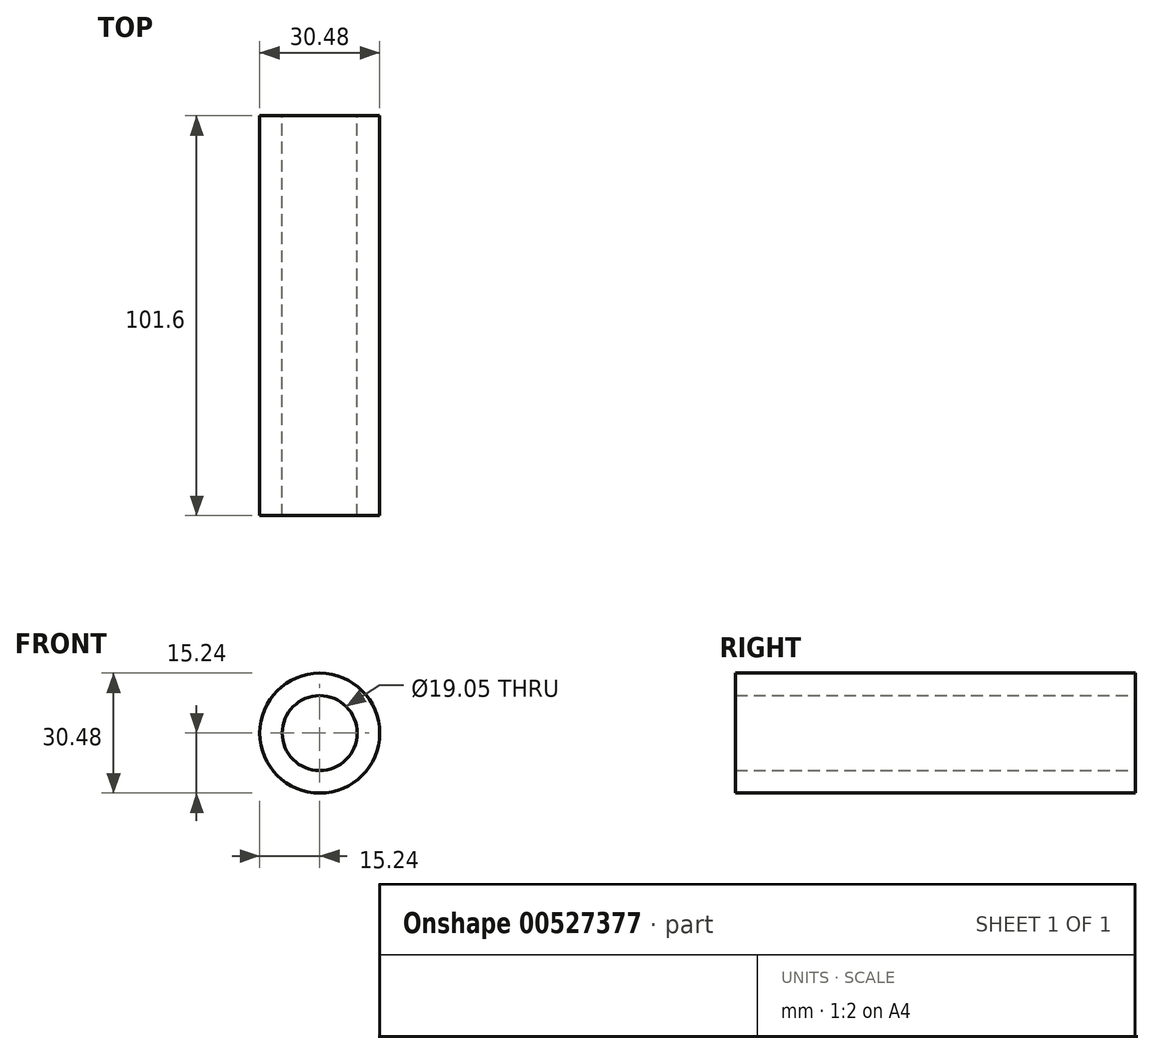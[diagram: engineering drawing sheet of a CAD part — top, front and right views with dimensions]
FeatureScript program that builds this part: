
annotation { "Feature Type Name" : "Feature", "Feature Type Description" : "" }
export const myFeature = defineFeature(function(context is Context, id is Id, definition is map)
    precondition{}
    {
        {
            var Q0;
            Q0=qCreatedBy(makeId("Front.planeOp"),FACE);
            var sketch = newSketch(context, id + "F0", { "sketchPlane" : qUnion([Q0])});
            skCircle(sketch, "E0", {"center": v(0, 0) * mm, "radius": 15.24 * mm});
            skCircle(sketch, "E1", {"center": v(0, 0) * mm, "radius": 9.53 * mm});
            skSolve(sketch);
        }
        {
            var Q0;
            Q0 = qSketchRegion(id + "F0", true);
            extrude(context, id + "F1", {"entities" : qUnion([Q0]), "depth" : 101.6 * mm, "offsetDistance" : 25.4 * mm});
        }
    });
